# Revit family: OASIS SHA-DM-4833 STD
name_source: partatom
category: Plumbing Fixtures
revit_build: Autodesk Revit 2013 (Build: 20130531_2115(x64)
units: mm (PartAtom-declared; Revit-internal decimal feet)

## types (5) — shared parameters
BIM Model by = www.epoch-design.com
Color = <By Category>
Grab Bar Finish = <By Category>
Manufacturer = OASIS
Sanitary Connector = Sanitary Connection
Seat Finish = <By Category>
Stainless Steel = <By Category>
Type Comments = SHOWER
URL = www.oasisbath.com

## per-type parameters (varying)
| type | Bar_Horz_Back_24 | Bar_Horz_Right | Bar_Vert | Model | Seat_Fold |
| Base Model | No | No | No | SHA-DM-4833 STD | No |
| BP1 package | Yes | Yes | No | SHA-DM-4833 STD/BP1 | No |
| BP2 package | Yes | Yes | Yes | SHA-DM-4833 STD/BP2 | No |
| TL package | Yes | Yes | No | SHA-DM-4833 STD/TL | Yes |
| TLV package | Yes | Yes | Yes | SHA-DM-4833 STD/TLV | Yes |

## geometry (parser evidence)
native form markers: Sweep x8
no freeform markers — native parametric forms only
